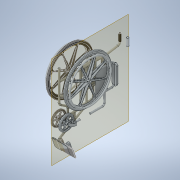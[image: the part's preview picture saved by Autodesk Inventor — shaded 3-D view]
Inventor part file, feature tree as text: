
AUTODESK INVENTOR PART (.ipt)
format: ipt  version: 2021 (Build 250183000, 183)  size: 1,127,424 bytes
history: native  units: mm
features: other x13, extrude x2, sketch x2, plane x1, mirror x1
ambient origin geometry x8: Origin, YZ Plane, XZ Plane, XY Plane, X Axis, Y Axis, Z Axis, Center Point
bodies: Solid1 (feature_tree), Solid2 (feature_tree), Solid5 (feature_tree), Solid7 (feature_tree), Solid10 (feature_tree), Solid11 (feature_tree), Solid13 (feature_tree), Solid17 (feature_tree), Solid18 (feature_tree), Solid19 (feature_tree), Solid20 (feature_tree), Solid24 (feature_tree), Solid26 (feature_tree)
feature tree (19):
  plane  "Work Plane1"
  extrude  "Extrusion1"  Depth=500.0mm TaperAngle=0.0deg
  mirror  "Mirror1"
  extrude  "Extrusion2"  [1 undecoded]
  sketch  "Sketch1"  dims[d0=50.0mm d1=500.0mm d2=0.0mm]
  sketch  "Sketch2"  dims[d3=10.0mm d4=0.0mm]
  other  "SideFrame_1:1"
  other  "SideFrame_1:2"
  other  "SideFrame_1:5"
  other  "SideFrame_1:7"
  other  "Arm_3:1"
  other  "Arm_3:2"
  other  "ArmPad_5:1"
  other  "WheelLarge_8:1"
  other  "WheelLarge_8:2"
  other  "WheelSmall_16:1"
  other  "CasterFork_17:1"
  other  "FootRest_12:1"
  other  "Grip_14:1"
note: 1 required parameter value undecoded (feature->parameter linkage not recoverable at this tier; creation-order binding heuristic only, values carry confidence <= 0.55)
